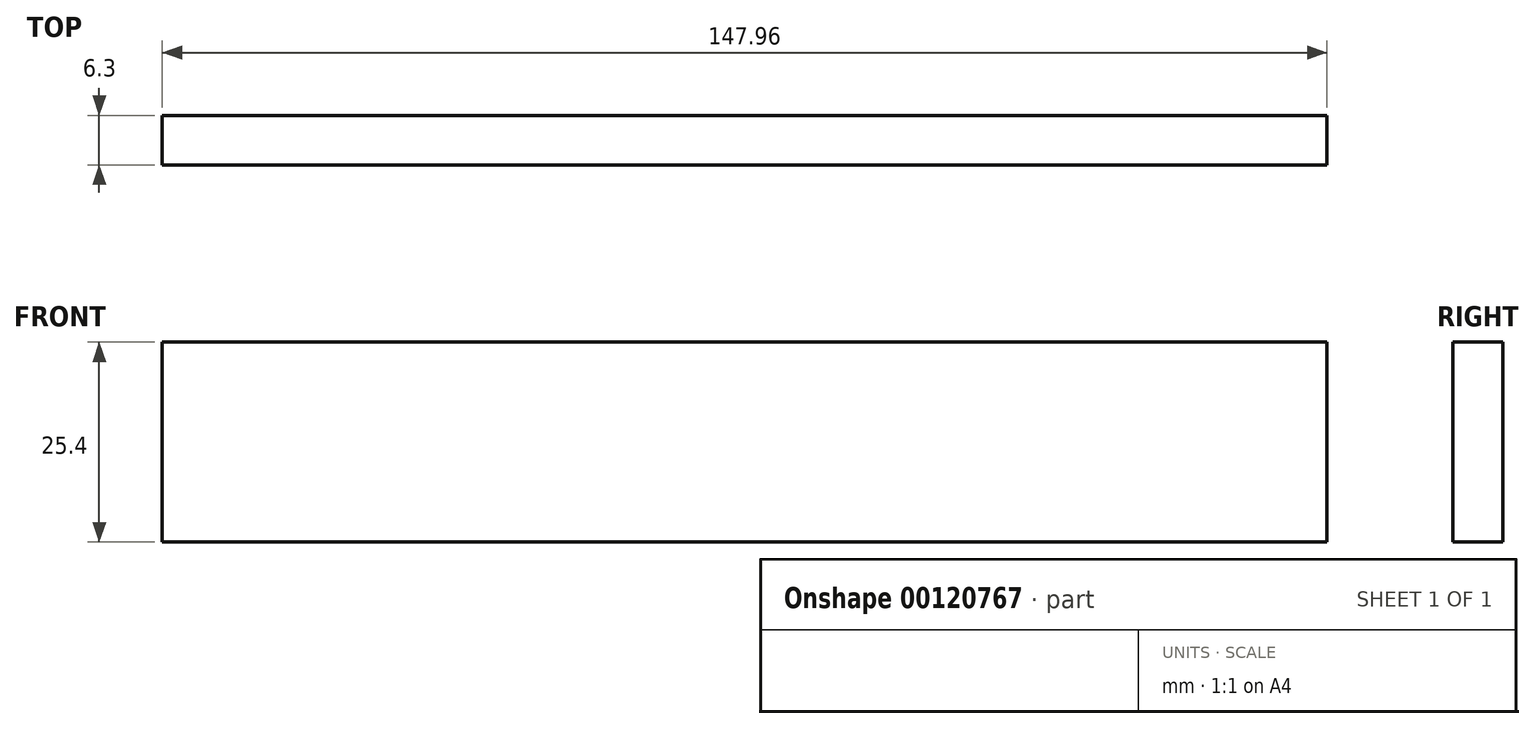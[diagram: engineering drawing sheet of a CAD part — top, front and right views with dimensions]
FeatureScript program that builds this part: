
annotation { "Feature Type Name" : "Feature", "Feature Type Description" : "" }
export const myFeature = defineFeature(function(context is Context, id is Id, definition is map)
    precondition{}
    {
        {
            var Q0;
            Q0=qCreatedBy(makeId("Top.planeOp"),FACE);
            var sketch = newSketch(context, id + "F0", { "sketchPlane" : qUnion([Q0])});
            skLineSegment(sketch, "E0.bottom", {"start": v(-73.98, 3.15) * mm, "end": v(73.98, 3.15) * mm});
            skLineSegment(sketch, "E0.top", {"start": v(-73.98, -3.15) * mm, "end": v(73.98, -3.15) * mm});
            skLineSegment(sketch, "E0.left", {"start": v(-73.98, 3.15) * mm, "end": v(-73.98, -3.15) * mm});
            skLineSegment(sketch, "E0.right", {"start": v(73.98, 3.15) * mm, "end": v(73.98, -3.15) * mm});
            skPoint(sketch, "E0.middle", {"position": v(0, 0) * mm});
            skSolve(sketch);
        }
        {
            var Q0;
            Q0=makeQuery(id+"F0.imprint","IMPRINT",FACE,{"disambiguationData":[TD([[makeQuery(id+"F0.imprint","IMPRINT",EDGE,{"derivedFrom":sQuery(id+"F0.wireOp",EDGE,"E0.bottom")}),-1.0]])]});
            extrude(context, id + "F1", {"entities" : qUnion([Q0]), "depth" : 25.4 * mm});
        }
    });
